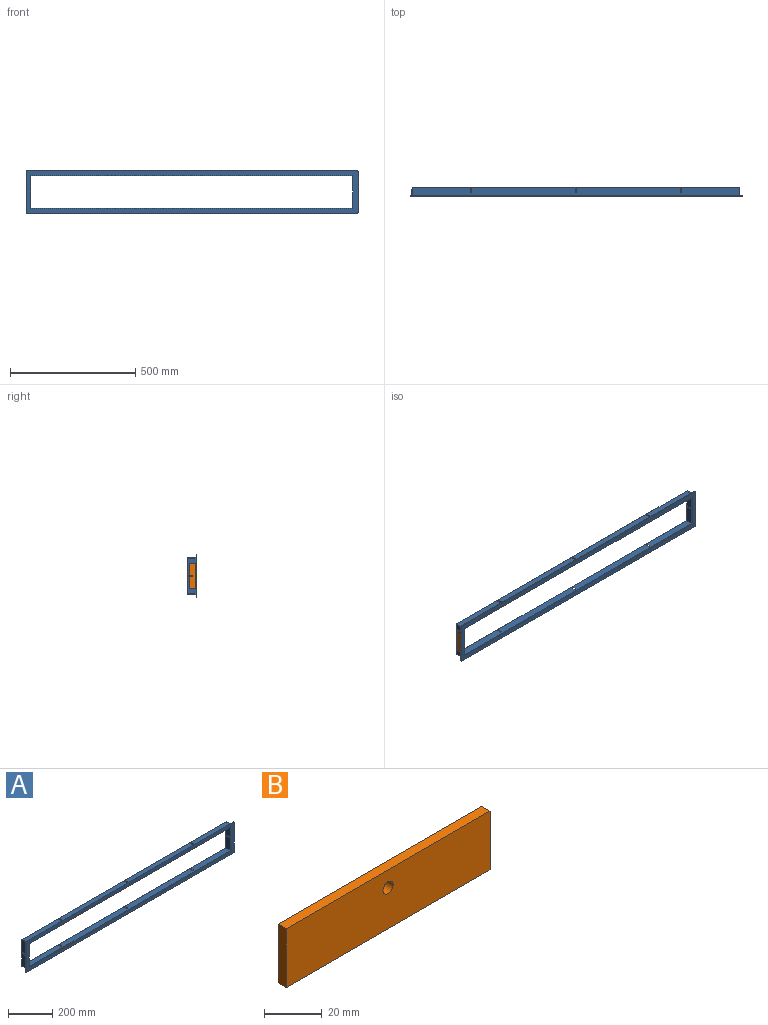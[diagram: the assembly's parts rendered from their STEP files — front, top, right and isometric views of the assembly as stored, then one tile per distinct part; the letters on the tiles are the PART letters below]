
ASSEMBLY  parts=2 mates=1
PART A: 56 faces, bbox 1328x38x170 mm
  f0: plane 1306x35mm, normal (0,0,1), area 45384.5mm2, adj f4,f7,f18,f19,f44,f45,f46,f47
  f1: plane 1306x35mm, normal (0,0,-1), area 45384.5mm2, adj f4,f7,f18,f19,f32,f33,f34,f35
  f2: plane 1300x35mm, normal (0,0,-1), area 45174.5mm2, adj f5,f6,f8,f19,f44,f45,f46,f47
  f3: plane 1300x35mm, normal (0,0,1), area 45174.5mm2, adj f5,f6,f8,f19,f32,f33,f34,f35
  f4: plane 148x35mm, normal (1,0,0), area 5071.5mm2, adj f0,f1,f18,f19,f28,f29,f30,f31
  f5: plane 142x35mm, normal (-1,0,0), area 4861.5mm2, adj f2,f3,f8,f19,f28,f29,f30,f31
  f6: plane 142x35mm, normal (1,0,0), area 4861.5mm2, adj f2,f3,f8,f19,f24,f25,f26,f27
  f7: plane 148x35mm, normal (-1,0,0), area 5071.5mm2, adj f0,f1,f18,f19,f24,f25,f26,f27
  f8: plane 1300x142mm, normal (0,1,0), area 17160mm2, adj f2,f3,f5,f6,f9,f10,f11,f16
  f9: plane 1288x3mm, normal (0,0,-1), area 3864mm2, adj f8,f10,f16,f17
  f10: plane 130x3mm, normal (-1,0,0), area 390mm2, adj f8,f9,f11,f17
  f11: plane 1288x3mm, normal (0,0,1), area 3864mm2, adj f8,f10,f16,f17
  f12: plane 166x3mm, normal (1,0,0), area 498mm2, adj f17,f18,f20,f23
  f13: plane 1324x3mm, normal (0,0,1), area 3972mm2, adj f17,f18,f20,f21
  f14: plane 166x3mm, normal (-1,0,0), area 498mm2, adj f17,f18,f21,f22
  f15: plane 1324x3mm, normal (0,0,-1), area 3972mm2, adj f17,f18,f22,f23
  f16: plane 130x3mm, normal (1,0,0), area 390mm2, adj f8,f9,f11,f17
  f17: plane 1328x170mm, normal (0,-1,0), area 58316.6mm2, adj f9,f10,f11,f12,f13,f14,f15,f16
  f18: plane 1328x170mm, normal (0,1,0), area 32468.6mm2, adj f0,f1,f4,f7,f12,f13,f14,f15
  f19: plane 1306x148mm, normal (0,1,0), area 8688mm2, adj f0,f1,f2,f3,f4,f5,f6,f7
  f20: cylinder r=2mm len=3mm, axis (0,-1,0), area 9.4mm2, adj f12,f13,f17,f18
  f21: cylinder r=2mm len=3mm, axis (0,1,0), area 9.4mm2, adj f13,f14,f17,f18
  f22: cylinder r=2mm len=3mm, axis (0,-1,0), area 9.4mm2, adj f14,f15,f17,f18
  f23: cylinder r=2mm len=3mm, axis (0,1,0), area 9.4mm2, adj f12,f15,f17,f18
  f24: cylinder r=3.5mm len=7mm, axis (1,0,0), area 33mm2, adj f6,f7,f25,f27
  f25: plane 10x3mm, normal (0,0,-1), area 30mm2, adj f6,f7,f24,f26
  f26: cylinder r=3.5mm len=7mm, axis (1,0,0), area 33mm2, adj f6,f7,f25,f27
  f27: plane 10x3mm, normal (0,0,1), area 30mm2, adj f6,f7,f24,f26
  f28: plane 10x3mm, normal (0,0,1), area 30mm2, adj f4,f5,f29,f31
  f29: cylinder r=3.5mm len=7mm, axis (1,0,0), area 33mm2, adj f4,f5,f28,f30
  f30: plane 10x3mm, normal (0,0,-1), area 30mm2, adj f4,f5,f29,f31
  f31: cylinder r=3.5mm len=7mm, axis (1,0,0), area 33mm2, adj f4,f5,f28,f30
  f32: cylinder r=3.5mm len=7mm, axis (0,0,1), area 33mm2, adj f1,f3,f33,f35
  f33: plane 10x3mm, normal (1,0,0), area 30mm2, adj f1,f3,f32,f34
  f34: cylinder r=3.5mm len=7mm, axis (0,0,1), area 33mm2, adj f1,f3,f33,f35
  f35: plane 10x3mm, normal (-1,0,0), area 30mm2, adj f1,f3,f32,f34
  f36: plane 10x3mm, normal (-1,0,0), area 30mm2, adj f1,f3,f37,f39
  f37: cylinder r=3.5mm len=7mm, axis (0,0,1), area 33mm2, adj f1,f3,f36,f38
  f38: plane 10x3mm, normal (1,0,0), area 30mm2, adj f1,f3,f37,f39
  f39: cylinder r=3.5mm len=7mm, axis (0,0,1), area 33mm2, adj f1,f3,f36,f38
  f40: cylinder r=3.5mm len=7mm, axis (0,0,1), area 33mm2, adj f1,f3,f41,f43
  f41: plane 10x3mm, normal (1,0,0), area 30mm2, adj f1,f3,f40,f42
  f42: cylinder r=3.5mm len=7mm, axis (0,0,1), area 33mm2, adj f1,f3,f41,f43
  f43: plane 10x3mm, normal (-1,0,0), area 30mm2, adj f1,f3,f40,f42
  f44: plane 10x3mm, normal (-1,0,0), area 30mm2, adj f0,f2,f45,f47
  f45: cylinder r=3.5mm len=7mm, axis (0,0,1), area 33mm2, adj f0,f2,f44,f46
  f46: plane 10x3mm, normal (1,0,0), area 30mm2, adj f0,f2,f45,f47
  f47: cylinder r=3.5mm len=7mm, axis (0,0,1), area 33mm2, adj f0,f2,f44,f46
  f48: cylinder r=3.5mm len=7mm, axis (0,0,1), area 33mm2, adj f0,f2,f49,f51
  f49: plane 10x3mm, normal (1,0,0), area 30mm2, adj f0,f2,f48,f50
  f50: cylinder r=3.5mm len=7mm, axis (0,0,1), area 33mm2, adj f0,f2,f49,f51
  f51: plane 10x3mm, normal (-1,0,0), area 30mm2, adj f0,f2,f48,f50
  f52: plane 10x3mm, normal (-1,0,0), area 30mm2, adj f0,f2,f53,f55
  f53: cylinder r=3.5mm len=7mm, axis (0,0,1), area 33mm2, adj f0,f2,f52,f54
  f54: plane 10x3mm, normal (1,0,0), area 30mm2, adj f0,f2,f53,f55
  f55: cylinder r=3.5mm len=7mm, axis (0,0,1), area 33mm2, adj f0,f2,f52,f54
PART B: 7 faces, bbox 100x4x25 mm
  f0: plane 25x4mm, normal (1,0,0), area 100mm2, adj f1,f3,f4,f5
  f1: plane 100x4mm, normal (0,0,1), area 400mm2, adj f0,f2,f4,f5
  f2: plane 25x4mm, normal (-1,0,0), area 100mm2, adj f1,f3,f4,f5
  f3: plane 100x4mm, normal (0,0,-1), area 400mm2, adj f0,f2,f4,f5
  f4: plane 100x25mm, normal (0,-1,0), area 2480.4mm2, adj f0,f1,f2,f3,f6
  f5: plane 100x25mm, normal (0,1,0), area 2480.4mm2, adj f0,f1,f2,f3,f6
  f6: cylinder r=2.5mm len=5mm, axis (0,-1,0), area 62.8mm2, adj f4,f5
PLACE A t=(25.8,-57.51,0)mm fixed
PLACE B rot(axis=(-0.58,0.58,0.58),120deg) t=(-631.2,-44.51,0)mm
MATE pin_slot B.f6 <-> A.f24  axis (1,0,0) through (-627.2,-39.51,0)mm
